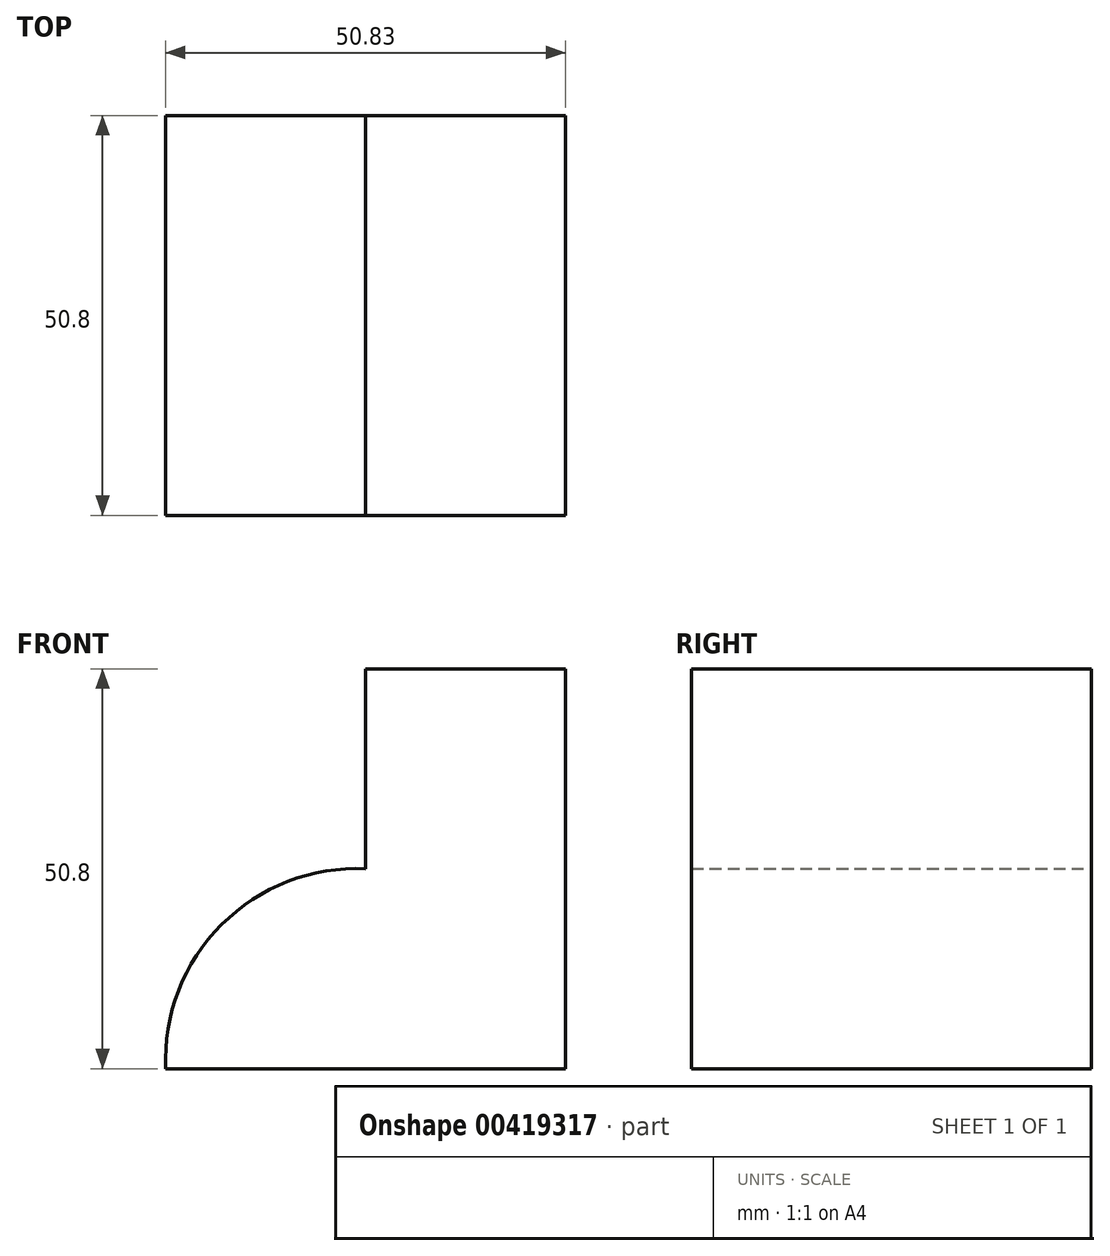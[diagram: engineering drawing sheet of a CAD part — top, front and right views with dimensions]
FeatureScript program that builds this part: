
annotation { "Feature Type Name" : "Feature", "Feature Type Description" : "" }
export const myFeature = defineFeature(function(context is Context, id is Id, definition is map)
    precondition{}
    {
        {
            var Q0;
            Q0=qCreatedBy(makeId("Front.planeOp"),FACE);
            var sketch = newSketch(context, id + "F0", { "sketchPlane" : qUnion([Q0])});
            skLineSegment(sketch, "E0", {"start": v(0, 0) * mm, "end": v(-50.8, 0) * mm});
            skLineSegment(sketch, "E1", {"start": v(0, 0) * mm, "end": v(0, 50.8) * mm});
            skLineSegment(sketch, "E2", {"start": v(0, 50.8) * mm, "end": v(-25.4, 50.8) * mm});
            skLineSegment(sketch, "E3", {"start": v(-25.4, 50.8) * mm, "end": v(-25.4, 25.4) * mm});
            skArc(sketch, "E4", {"start": v(-25.4, 25.4) * mm, "mid": v(-43.7, 18.3) * mm, "end": v(-50.8, 0) * mm});
            skSolve(sketch);
        }
        {
            var Q0;
            Q0=makeQuery(id+"F0.imprint","IMPRINT",FACE,{"disambiguationData":[TD([[makeQuery(id+"F0.imprint","IMPRINT",EDGE,{"derivedFrom":sQuery(id+"F0.wireOp",EDGE,"E0")}),-1.0]])]});
            extrude(context, id + "F1", {"entities" : qUnion([Q0]), "depth" : 50.8 * mm});
        }
    });
